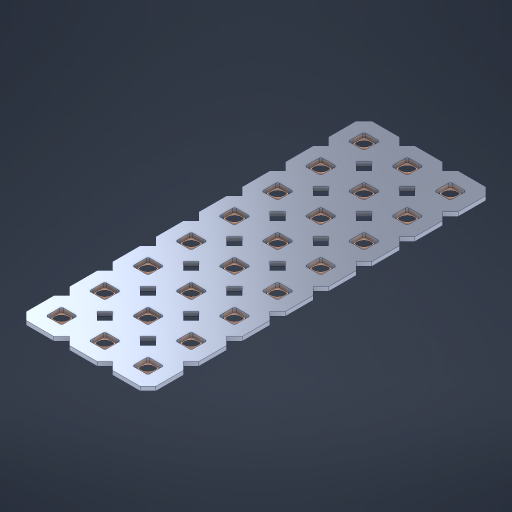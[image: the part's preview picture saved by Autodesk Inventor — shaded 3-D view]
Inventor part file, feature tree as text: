
AUTODESK INVENTOR PART (.ipt)
format: ipt  version: 2023 (Build 270158000, 158)  size: 534,528 bytes
history: native  units: in
note: dims shown in document units (in); Inventor stores cm internally (conversion verified against a paired STEP export)
features: other x25, extrude x23, sketch x2, pattern_linear x1
ambient origin geometry x8: Origin, YZ Plane, XZ Plane, XY Plane, X Axis, Y Axis, Z Axis, Center Point
bodies: Solid1 (feature_tree), Body (feature_tree)
feature tree (51):
  pattern_linear  "Rectangular Pattern1"  Spacing1=0.09in  [1 undecoded]
  sketch  "Sketch1"  dims[d1=0.5in]
  sketch  "Sketch2"  dims[d2=0.182in d3=0.09in d4=0.09in d5=0.09in d6=0.09in d7=0.09in d8=0.09in d9=0.09in d10=0.09in d11=0.02in d13=0.0in d14=0.172in d15=0.0625in d16=0.0in d19=0.5in d22=0.5in]
  other  "Srf1"
  other  "Srf126"
  other  "Srf127"
  other  "Srf128"
  other  "Srf129"
  other  "Srf130"
  other  "Srf131"
  other  "Srf250"
  other  "Srf268"
  other  "Srf269"
  other  "Srf270"
  other  "Srf271"
  other  "Srf272"
  other  "Srf273"
  other  "Srf274"
  other  "Srf275"
  other  "Srf293"
  other  "Srf294"
  other  "Srf295"
  other  "Srf296"
  other  "Srf297"
  other  "Srf298"
  other  "Srf299"
  other  "Srf300"
  other  "Circle"
  extrude  "ExtrusionSrf126"  Depth=0.09in
  extrude  "ExtrusionSrf127"  Depth=0.09in
  extrude  "ExtrusionSrf128"  Depth=0.09in
  extrude  "ExtrusionSrf129"  Depth=0.09in
  extrude  "ExtrusionSrf130"  Depth=0.09in
  extrude  "ExtrusionSrf131"  Depth=0.09in
  extrude  "ExtrusionSrf250"  Depth=0.09in
  extrude  "ExtrusionSrf268"  Depth=0.02in
  extrude  "ExtrusionSrf269"  TaperAngle=0.0deg  [1 undecoded]
  extrude  "ExtrusionSrf270"  Depth=0.5in
  extrude  "ExtrusionSrf271"  Depth=0.5in TaperAngle=0.0deg
  extrude  "ExtrusionSrf272"  Depth=0.5in
  extrude  "ExtrusionSrf273"  Depth=0.5in
  extrude  "ExtrusionSrf274"  [1 undecoded]
  extrude  "ExtrusionSrf275"  [1 undecoded]
  extrude  "ExtrusionSrf293"  [1 undecoded]
  extrude  "ExtrusionSrf294"  [1 undecoded]
  extrude  "ExtrusionSrf295"  [1 undecoded]
  extrude  "ExtrusionSrf296"  [1 undecoded]
  extrude  "ExtrusionSrf297"  [1 undecoded]
  extrude  "ExtrusionSrf298"  [1 undecoded]
  extrude  "ExtrusionSrf299"  [1 undecoded]
  extrude  "ExtrusionSrf300"  [1 undecoded]
note: 12 required parameter values undecoded (feature->parameter linkage not recoverable at this tier; creation-order binding heuristic only, values carry confidence <= 0.55)
